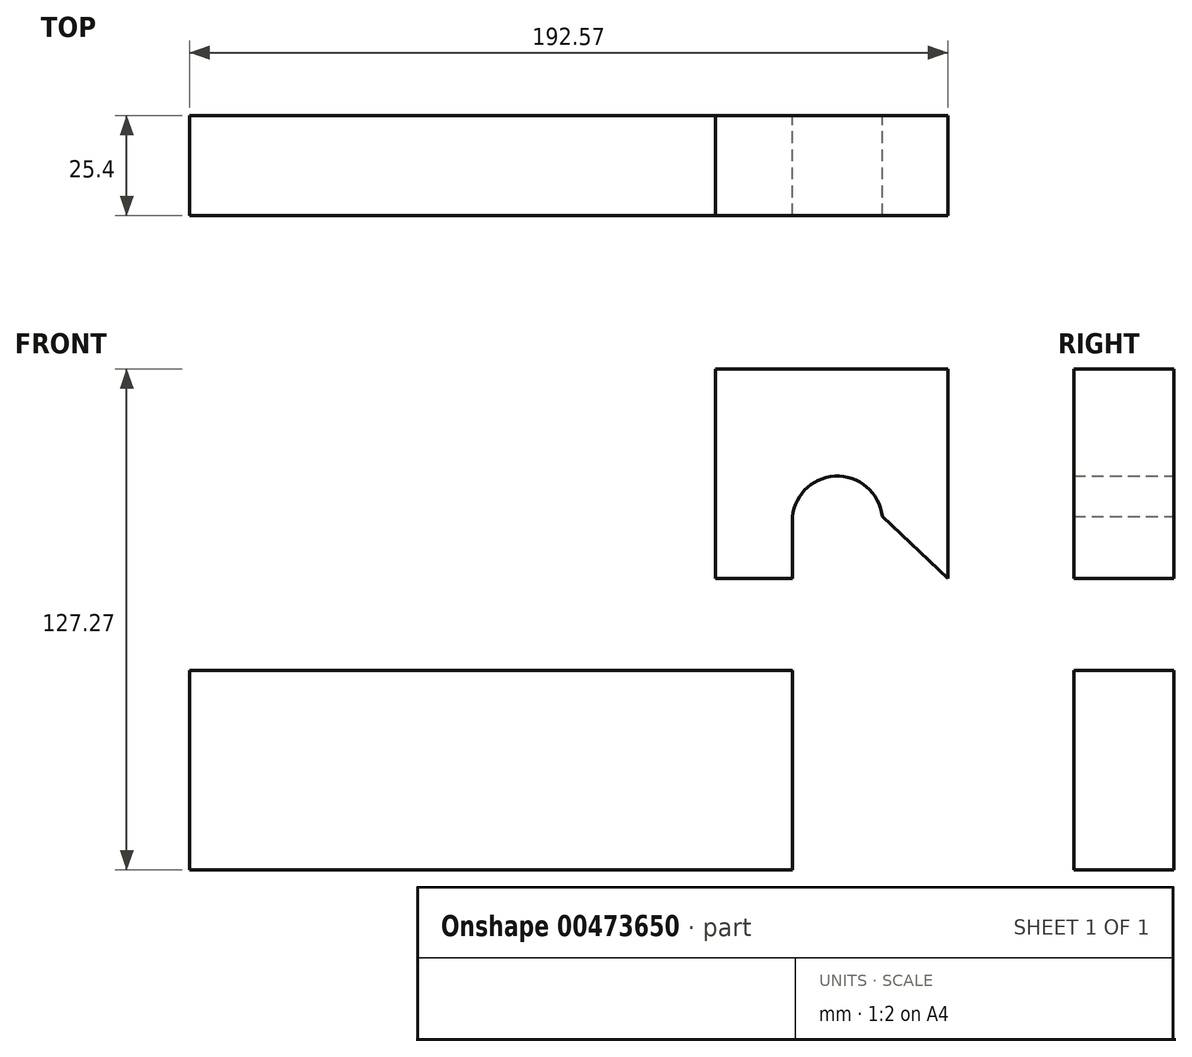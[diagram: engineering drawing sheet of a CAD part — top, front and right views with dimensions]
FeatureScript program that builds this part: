
annotation { "Feature Type Name" : "Feature", "Feature Type Description" : "" }
export const myFeature = defineFeature(function(context is Context, id is Id, definition is map)
    precondition{}
    {
        {
            var Q0;
            Q0=qCreatedBy(makeId("Front.planeOp"),FACE);
            var sketch = newSketch(context, id + "F0", { "sketchPlane" : qUnion([Q0])});
            skLineSegment(sketch, "E0.bottom", {"start": v(-76.53, 25.37) * mm, "end": v(76.53, 25.37) * mm});
            skLineSegment(sketch, "E0.top", {"start": v(-76.53, -25.37) * mm, "end": v(76.53, -25.37) * mm});
            skLineSegment(sketch, "E0.left", {"start": v(-76.53, 25.37) * mm, "end": v(-76.53, -25.37) * mm});
            skLineSegment(sketch, "E0.right", {"start": v(76.53, 25.37) * mm, "end": v(76.53, -25.37) * mm});
            skPoint(sketch, "E0.middle", {"position": v(0, 0) * mm});
            skLineSegment(sketch, "E1.bottom", {"start": v(116.04, 48.66) * mm, "end": v(56.98, 48.66) * mm});
            skLineSegment(sketch, "E1.top", {"start": v(116.04, 101.9) * mm, "end": v(56.98, 101.9) * mm});
            skLineSegment(sketch, "E1.left", {"start": v(116.04, 48.66) * mm, "end": v(116.04, 101.9) * mm});
            skLineSegment(sketch, "E1.right", {"start": v(56.98, 48.66) * mm, "end": v(56.98, 101.9) * mm});
            skPoint(sketch, "E1.middle", {"position": v(86.5, 75.28) * mm});
            skLineSegment(sketch, "E2", {"start": v(76.53, 25.37) * mm, "end": v(76.53, 63.22) * mm});
            skArc(sketch, "E3", {"start": v(76.53, 63.22) * mm, "mid": v(87.37, 74.67) * mm, "end": v(99.4, 64.46) * mm});
            skLineSegment(sketch, "E4", {"start": v(99.4, 64.46) * mm, "end": v(116.04, 48.66) * mm});
            skSolve(sketch);
        }
        {
            var Q0;
            Q0=makeQuery(id+"F0.imprint","IMPRINT",FACE,{"disambiguationData":[TD([[makeQuery(id+"F0.imprint","IMPRINT",EDGE,{"derivedFrom":sQuery(id+"F0.wireOp",EDGE,"E0.bottom")}),-1.0]])]});
            var sketch = newSketch(context, id + "F1", { "sketchPlane" : qUnion([Q0])});
            skSolve(sketch);
        }
        {
            var Q0;
            Q0=makeQuery(id+"F0.imprint","IMPRINT",FACE,{"disambiguationData":[TD([[makeQuery(id+"F0.imprint","IMPRINT",EDGE,{"derivedFrom":sQuery(id+"F0.wireOp",EDGE,"E0.bottom")}),-1.0]])]});
            var Q1;
            {var subQ4=sQuery(id+"F0.wireOp",EDGE,"E3");Q1=makeQuery(id+"F0.imprint","IMPRINT",FACE,{"disambiguationData":[TD([[makeQuery(id+"F0.imprint","IMPRINT",EDGE,{"derivedFrom":subQ4}),-1.0]])]});}
            var Q2;
            Q2=makeQuery(id+"F0.imprint","IMPRINT",FACE,{"disambiguationData":[TD([[makeQuery(id+"F0.imprint","IMPRINT",EDGE,{"derivedFrom":sQuery(id+"F0.wireOp",EDGE,"E1.top")}),1.0]])]});
            var Q3;
            Q3=makeQuery(id+"F1.imprint","IMPRINT",FACE,{"disambiguationData":[TD([[makeQuery(id+"F1.imprint","IMPRINT",EDGE,{"derivedFrom":makeQuery(id+"F0.imprint","IMPRINT",EDGE,{"derivedFrom":sQuery(id+"F0.wireOp",EDGE,"E0.bottom")})}),-1.0]])]});
            extrude(context, id + "F2", {"entities" : qUnion([Q0, Q1, Q2, Q3]), "depth" : 25.4 * mm});
        }
    });
